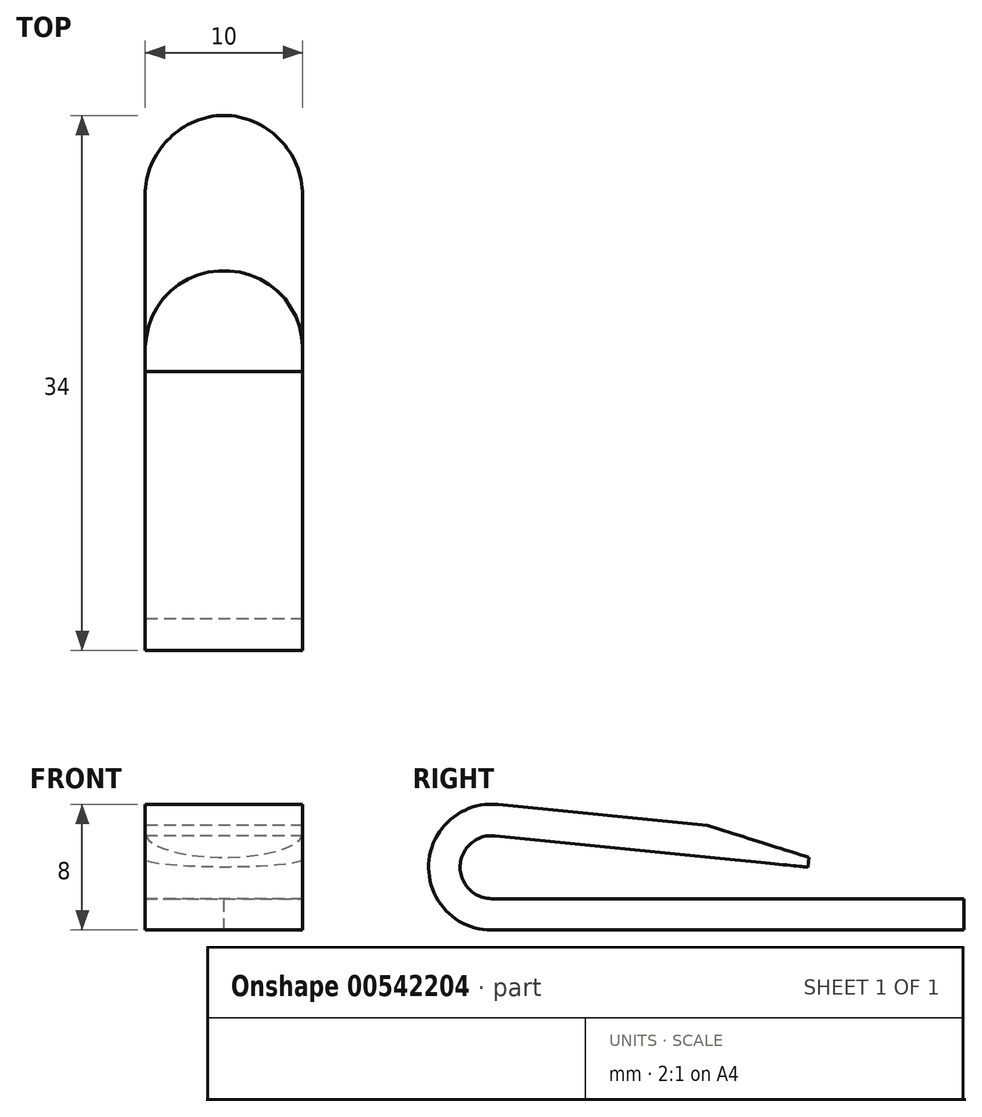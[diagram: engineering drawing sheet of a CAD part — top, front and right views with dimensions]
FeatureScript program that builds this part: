
annotation { "Feature Type Name" : "Feature", "Feature Type Description" : "" }
export const myFeature = defineFeature(function(context is Context, id is Id, definition is map)
    precondition{}
    {
        {
            var Q0;
            Q0=qCreatedBy(makeId("Right.planeOp"),FACE);
            var sketch = newSketch(context, id + "F0", { "sketchPlane" : qUnion([Q0])});
            skLineSegment(sketch, "E0", {"start": v(11.97, 0) * mm, "end": v(-18.03, 0) * mm});
            skArc(sketch, "E1", {"start": v(-17.83, 4) * mm, "mid": v(-20.03, 2.1) * mm, "end": v(-18.03, 0) * mm});
            skLineSegment(sketch, "E2", {"start": v(-17.83, 4) * mm, "end": v(2.07, 2) * mm});
            skLineSegment(sketch, "E3.0", {"start": v(-17.63, 5.98) * mm, "end": v(-4.31, 4.65) * mm});
            skArc(sketch, "E3.1", {"start": v(-17.63, 5.98) * mm, "mid": v(-22.02, 2.2) * mm, "end": v(-18.03, -2) * mm});
            skLineSegment(sketch, "E3.2", {"start": v(11.97, -2) * mm, "end": v(-18.03, -2) * mm});
            skLineSegment(sketch, "E4", {"start": v(2.07, 2) * mm, "end": v(2.13, 2.62) * mm});
            skLineSegment(sketch, "E5", {"start": v(11.97, -2) * mm, "end": v(11.97, 0) * mm});
            skLineSegment(sketch, "E6", {"start": v(2.13, 2.62) * mm, "end": v(-4.31, 4.65) * mm});
            skSolve(sketch);
        }
        {
            var Q0;
            Q0=makeQuery(id+"F0.imprint","IMPRINT",FACE,{"disambiguationData":[TD([[makeQuery(id+"F0.imprint","IMPRINT",EDGE,{"derivedFrom":sQuery(id+"F0.wireOp",EDGE,"E0")}),1.0]])]});
            extrude(context, id + "F1", {"entities" : qUnion([Q0]), "endBound" : BoundingType.SYMMETRIC, "depth" : 10 * mm, "offsetDistance" : 25 * mm});
        }
        {
            var Q0;
            Q0=makeQuery(id+"F1.opExtrude","CAP_EDGE",EDGE,{"disambiguationData":[OSD([sQuery(id+"F0.wireOp",EDGE,"E5")])],"isStart":false});
            var Q1;
            Q1=makeQuery(id+"F1.opExtrude","CAP_EDGE",EDGE,{"disambiguationData":[OSD([sQuery(id+"F0.wireOp",EDGE,"E5")])],"isStart":true});
            chamfer(context, id + "F2", {"entities" : qUnion([Q0, Q1]), "width" : 3 * mm, "tangentPropagation" : true});
        }
        {
            var Q0;
            {var subQ0=sQuery(id+"F0.wireOp",EDGE,"E5");Q0=makeQuery(id+"F2.opChamfer","BLEND_EDGE",EDGE,{"blendedFrom":[makeQuery(id+"F1.opExtrude","CAP_EDGE",EDGE,{"disambiguationData":[OSD([subQ0])],"isStart":true}),makeQuery(id+"F1.opExtrude","CAP_FACE",FACE,{"disambiguationData":[OSD([sQuery(id+"F0.wireOp",EDGE,"E0"),sQuery(id+"F0.wireOp",EDGE,"E1"),sQuery(id+"F0.wireOp",EDGE,"E2"),sQuery(id+"F0.wireOp",EDGE,"E3.0"),sQuery(id+"F0.wireOp",EDGE,"E3.1"),sQuery(id+"F0.wireOp",EDGE,"E3.2"),sQuery(id+"F0.wireOp",EDGE,"E4"),subQ0,sQuery(id+"F0.wireOp",EDGE,"E6")])],"isStart":true})],"blendedInto":[makeQuery(id+"F1.opExtrude","CAP_FACE",FACE,{"disambiguationData":[OSD([sQuery(id+"F0.wireOp",EDGE,"E0"),sQuery(id+"F0.wireOp",EDGE,"E1"),sQuery(id+"F0.wireOp",EDGE,"E2"),sQuery(id+"F0.wireOp",EDGE,"E3.0"),sQuery(id+"F0.wireOp",EDGE,"E3.1"),sQuery(id+"F0.wireOp",EDGE,"E3.2"),sQuery(id+"F0.wireOp",EDGE,"E4"),subQ0,sQuery(id+"F0.wireOp",EDGE,"E6")])],"isStart":true})]});}
            var Q1;
            {var subQ0=sQuery(id+"F0.wireOp",EDGE,"E5");Q1=makeQuery(id+"F2.opChamfer","BLEND_EDGE",EDGE,{"blendedFrom":[makeQuery(id+"F1.opExtrude","CAP_EDGE",EDGE,{"disambiguationData":[OSD([subQ0])],"isStart":true}),makeQuery(id+"F1.opExtrude","SWEPT_FACE",FACE,{"disambiguationData":[OSD([subQ0])]})],"blendedInto":[makeQuery(id+"F1.opExtrude","SWEPT_FACE",FACE,{"disambiguationData":[OSD([subQ0])]})]});}
            var Q2;
            {var subQ0=sQuery(id+"F0.wireOp",EDGE,"E5");Q2=makeQuery(id+"F2.opChamfer","BLEND_EDGE",EDGE,{"blendedFrom":[makeQuery(id+"F1.opExtrude","CAP_EDGE",EDGE,{"disambiguationData":[OSD([subQ0])],"isStart":false}),makeQuery(id+"F1.opExtrude","SWEPT_FACE",FACE,{"disambiguationData":[OSD([subQ0])]})],"blendedInto":[makeQuery(id+"F1.opExtrude","SWEPT_FACE",FACE,{"disambiguationData":[OSD([subQ0])]})]});}
            var Q3;
            {var subQ0=sQuery(id+"F0.wireOp",EDGE,"E5");Q3=makeQuery(id+"F2.opChamfer","BLEND_EDGE",EDGE,{"blendedFrom":[makeQuery(id+"F1.opExtrude","CAP_EDGE",EDGE,{"disambiguationData":[OSD([subQ0])],"isStart":false}),makeQuery(id+"F1.opExtrude","CAP_FACE",FACE,{"disambiguationData":[OSD([sQuery(id+"F0.wireOp",EDGE,"E0"),sQuery(id+"F0.wireOp",EDGE,"E1"),sQuery(id+"F0.wireOp",EDGE,"E2"),sQuery(id+"F0.wireOp",EDGE,"E3.0"),sQuery(id+"F0.wireOp",EDGE,"E3.1"),sQuery(id+"F0.wireOp",EDGE,"E3.2"),sQuery(id+"F0.wireOp",EDGE,"E4"),subQ0,sQuery(id+"F0.wireOp",EDGE,"E6")])],"isStart":false})],"blendedInto":[makeQuery(id+"F1.opExtrude","CAP_FACE",FACE,{"disambiguationData":[OSD([sQuery(id+"F0.wireOp",EDGE,"E0"),sQuery(id+"F0.wireOp",EDGE,"E1"),sQuery(id+"F0.wireOp",EDGE,"E2"),sQuery(id+"F0.wireOp",EDGE,"E3.0"),sQuery(id+"F0.wireOp",EDGE,"E3.1"),sQuery(id+"F0.wireOp",EDGE,"E3.2"),sQuery(id+"F0.wireOp",EDGE,"E4"),subQ0,sQuery(id+"F0.wireOp",EDGE,"E6")])],"isStart":false})]});}
            var Q4;
            Q4=makeQuery(id+"F1.opExtrude","CAP_EDGE",EDGE,{"disambiguationData":[OSD([sQuery(id+"F0.wireOp",EDGE,"E4")])],"isStart":true});
            var Q5;
            Q5=makeQuery(id+"F1.opExtrude","CAP_EDGE",EDGE,{"disambiguationData":[OSD([sQuery(id+"F0.wireOp",EDGE,"E4")])],"isStart":false});
            fillet(context, id + "F3", {"entities" : qUnion([Q0, Q1, Q2, Q3, Q4, Q5]), "radius" : 5 * mm, "tangentPropagation" : true, "allowEdgeOverflow" : false});
        }
    });
